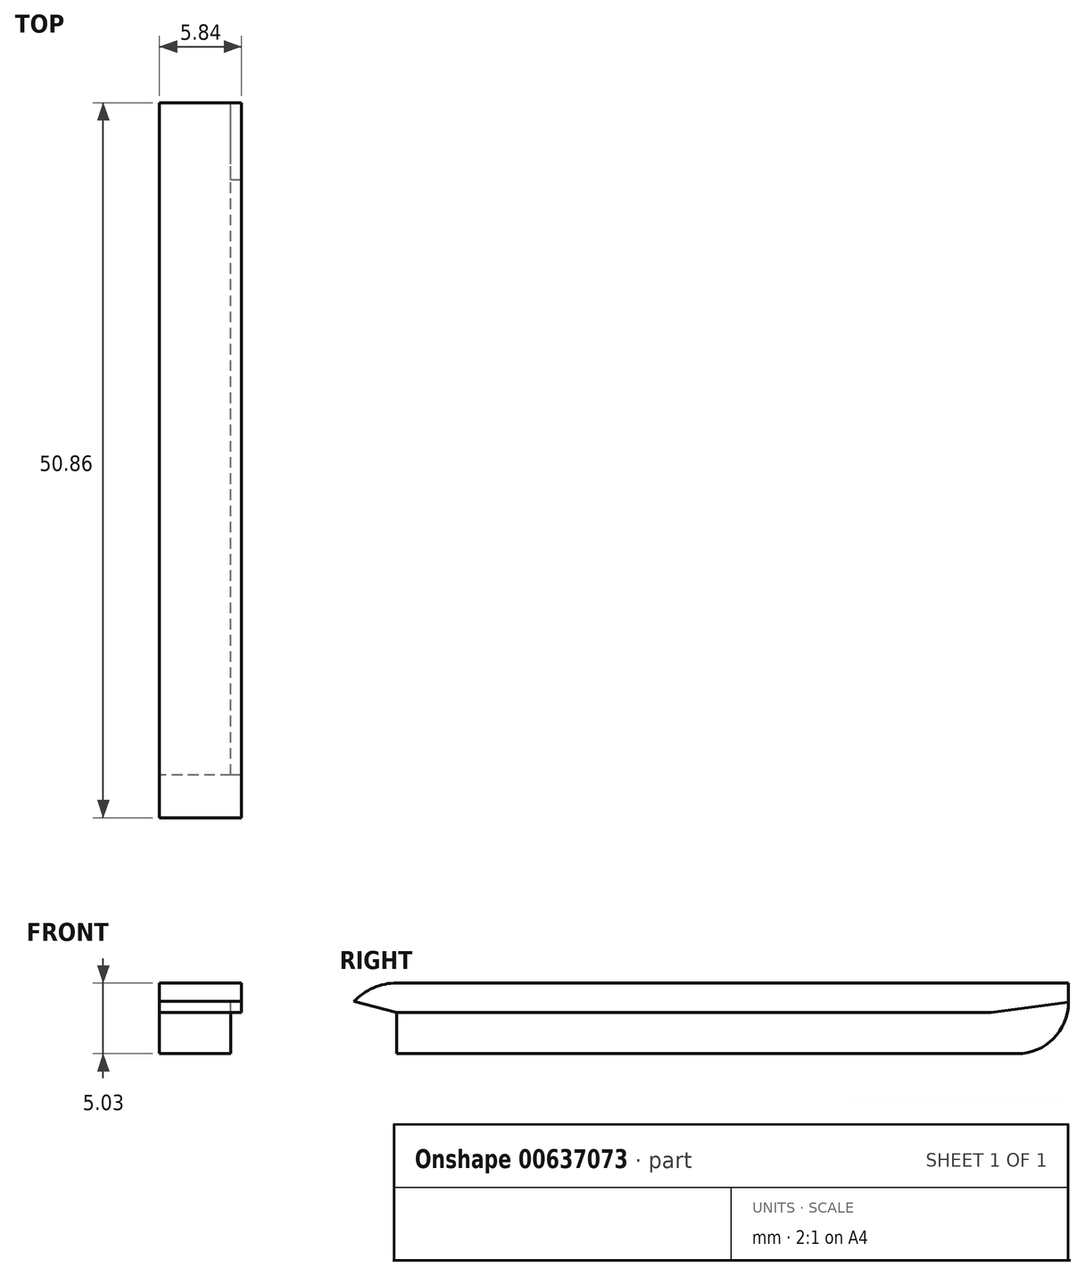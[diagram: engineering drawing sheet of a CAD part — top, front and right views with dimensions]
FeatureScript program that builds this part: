
annotation { "Feature Type Name" : "Feature", "Feature Type Description" : "" }
export const myFeature = defineFeature(function(context is Context, id is Id, definition is map)
    precondition{}
    {
        {
            var Q0;
            Q0=qCreatedBy(makeId("Right.planeOp"),FACE);
            var sketch = newSketch(context, id + "F0", { "sketchPlane" : qUnion([Q0])});
            skLineSegment(sketch, "E0", {"start": v(-27.86, 2.08) * mm, "end": v(14.45, 2.08) * mm});
            skArc(sketch, "E1", {"start": v(-27.86, 2.08) * mm, "mid": v(-29.52, 1.74) * mm, "end": v(-30.9, 0.77) * mm});
            skLineSegment(sketch, "E2", {"start": v(-30.9, 0.77) * mm, "end": v(-27.86, -0.01) * mm});
            skLineSegment(sketch, "E3", {"start": v(-27.86, 2.08) * mm, "end": v(-27.86, -2.95) * mm});
            skLineSegment(sketch, "E4", {"start": v(-27.86, -2.95) * mm, "end": v(14.45, -2.95) * mm});
            skArc(sketch, "E5", {"start": v(-27.86, -2.95) * mm, "mid": v(-30.18, -1.82) * mm, "end": v(-30.7, 0.71) * mm});
            skLineSegment(sketch, "E6", {"start": v(19.45, 2.08) * mm, "end": v(14.45, 2.08) * mm});
            skLineSegment(sketch, "E7", {"start": v(-27.86, -0.01) * mm, "end": v(14.45, -0.01) * mm});
            skLineSegment(sketch, "E8", {"start": v(14.45, -0.01) * mm, "end": v(14.45, 2.08) * mm});
            skLineSegment(sketch, "E9", {"start": v(14.45, -0.01) * mm, "end": v(14.45, -2.95) * mm});
            skArc(sketch, "E10", {"start": v(16.29, -2.95) * mm, "mid": v(18.88, -1.88) * mm, "end": v(19.95, 0.71) * mm});
            skLineSegment(sketch, "E11", {"start": v(16.29, -2.95) * mm, "end": v(14.45, -2.95) * mm});
            skLineSegment(sketch, "E12", {"start": v(14.45, -0.01) * mm, "end": v(19.95, 0.71) * mm});
            skLineSegment(sketch, "E13", {"start": v(19.95, 0.71) * mm, "end": v(19.95, 2.08) * mm});
            skLineSegment(sketch, "E14", {"start": v(19.95, 2.08) * mm, "end": v(19.45, 2.08) * mm});
            skSolve(sketch);
        }
        {
            var Q0;
            {var subQ0=sQuery(id+"F0.wireOp",EDGE,"E1");Q0=makeQuery(id+"F0.imprint","IMPRINT",FACE,{"disambiguationData":[TD([[makeQuery(id+"F0.imprint","IMPRINT",EDGE,{"derivedFrom":subQ0}),1.0]])]});}
            var Q1;
            {var subQ0=sQuery(id+"F0.wireOp",EDGE,"E0");Q1=makeQuery(id+"F0.imprint","IMPRINT",FACE,{"disambiguationData":[TD([[makeQuery(id+"F0.imprint","IMPRINT",EDGE,{"derivedFrom":subQ0}),-1.0]])]});}
            var Q2;
            Q2=makeQuery(id+"F0.imprint","IMPRINT",FACE,{"disambiguationData":[TD([[makeQuery(id+"F0.imprint","IMPRINT",EDGE,{"derivedFrom":sQuery(id+"F0.wireOp",EDGE,"E6")}),1.0]])]});
            extrude(context, id + "F1", {"entities" : qUnion([Q0, Q1, Q2]), "depth" : 5.84 * mm, "offsetDistance" : 25.4 * mm});
        }
        {
            var Q0;
            {var subQ3=sQuery(id+"F0.wireOp",EDGE,"E5");Q0=makeQuery(id+"F0.imprint","IMPRINT",FACE,{"disambiguationData":[TD([[makeQuery(id+"F0.imprint","IMPRINT",EDGE,{"derivedFrom":subQ3}),-1.0]])]});}
            var Q1;
            {var subQ2=sQuery(id+"F0.wireOp",EDGE,"E4");Q1=makeQuery(id+"F0.imprint","IMPRINT",FACE,{"disambiguationData":[TD([[makeQuery(id+"F0.imprint","IMPRINT",EDGE,{"derivedFrom":subQ2}),1.0]])]});}
            var Q2;
            Q2=makeQuery(id+"F0.imprint","IMPRINT",FACE,{"disambiguationData":[TD([[makeQuery(id+"F0.imprint","IMPRINT",EDGE,{"derivedFrom":sQuery(id+"F0.wireOp",EDGE,"E9")}),1.0]])]});
            extrude(context, id + "F2", {"entities" : qUnion([Q0, Q1, Q2]), "operationType" : NewBodyOperationType.ADD, "depth" : 5.08 * mm, "offsetDistance" : 25.4 * mm});
        }
    });
